# Revit family: Plumbing_Valves_Bermad_750-80_Level_Control_Valve_with_Altitude Pilot Threaded 1.5in-3in
name_source: partatom
category: Pipe Accessories
units: mm (PartAtom-declared; Revit-internal decimal feet)

## family parameters
Always vertical = Yes
Cut with Voids When Loaded = No
Part Type = Valve - Breaks Into
Round Connector Dimension = Use Diameter
Shared = No
Work Plane-Based = No

## types (4) — shared parameters
700EN = No
700ES = No
700Grooved = No
700Threaded = Yes
Act_Ang = 25.00°
Assembly Code = D2020300
D_Table = 700 Revit Sizes
D_Table_Version = 2
Date of publishing = 03/10/2019
Description = Level Control Valve with Altitude Pilot
HC = No
M = 160 mm
Manufacturer = Bermad
Max Working Water Pressure = 27.6 bar
Max Working Water Temperature = 60 °C
Model = 750-80
PA = No
PA_8 = Yes
PB = No
PBL = No
Port_Dim = 40 mm  [stored 0.131234 ft]
Product url = www.bermad.com/product/bc-750-80-p
Show Actuator Maintenance Space = No
T_from_port = 220 mm
URL = www.Bermad.com
Valve Seires = 700 Threaded

## per-type parameters (varying)
- 1.5" - DN40: Act_BD=119 mm; Ax=18 mm  [stored 0.0590551 ft]; Ay=80 mm  [stored 0.262467 ft]; Body_Dim=70 mm  [stored 0.229659 ft]; C_Plus=98 mm  [stored 0.321522 ft]; D1=86 mm  [stored 0.282152 ft]; D2=125 mm; D3=85 mm  [stored 0.278871 ft]; D4=125 mm; D5=86 mm  [stored 0.282152 ft]; D6=38 mm  [stored 0.124672 ft]; Flange_Dim=75 mm  [stored 0.246063 ft]; Flange_Thick=12 mm  [stored 0.0393701 ft]; H=201 mm; H1=10 mm  [stored 0.0328084 ft]; H2=19 mm  [stored 0.062336 ft]; H3=12 mm  [stored 0.0393701 ft]; H4=32 mm  [stored 0.104987 ft]; H5=9 mm  [stored 0.0295276 ft]; K Coefficient=3.1; L=155 mm; L_Half=78 mm  [stored 0.255906 ft]; Nominal Diameter=40 mm  [stored 0.131234 ft]; Port_Downx=36 mm  [stored 0.11811 ft]; Port_Upx=37 mm  [stored 0.121391 ft]; Port_W=41 mm  [stored 0.134514 ft]; Port_W2=81 mm  [stored 0.265748 ft]; Port_h=37 mm  [stored 0.121391 ft]; W=129 mm; Weight=0.05 kN; h=37 mm  [stored 0.121391 ft]
- 2" - DN50: Act_BD=119 mm; Ax=16 mm  [stored 0.0524934 ft]; Ay=82 mm  [stored 0.269029 ft]; Body_Dim=75 mm  [stored 0.246063 ft]; C_Plus=98 mm  [stored 0.321522 ft]; D1=86 mm  [stored 0.282152 ft]; D2=125 mm; D3=85 mm  [stored 0.278871 ft]; D4=125 mm; D5=86 mm  [stored 0.282152 ft]; D6=38 mm  [stored 0.124672 ft]; Flange_Dim=80 mm  [stored 0.262467 ft]; Flange_Thick=13 mm; H=203 mm; H1=10 mm  [stored 0.0328084 ft]; H2=19 mm  [stored 0.062336 ft]; H3=12 mm  [stored 0.0393701 ft]; H4=32 mm  [stored 0.104987 ft]; H5=9 mm  [stored 0.0295276 ft]; K Coefficient=5.4; L=155 mm; L_Half=78 mm  [stored 0.255906 ft]; Nominal Diameter=50 mm  [stored 0.164042 ft]; Port_Downx=37 mm  [stored 0.121391 ft]; Port_Upx=37 mm  [stored 0.121391 ft]; Port_W=41 mm  [stored 0.134514 ft]; Port_W2=81 mm  [stored 0.265748 ft]; Port_h=40 mm  [stored 0.131234 ft]; W=129 mm; Weight=0.05 kN; h=40 mm  [stored 0.131234 ft]
- 2.5" - DN65: Act_BD=119 mm; Ax=4 mm  [stored 0.0131234 ft]; Ay=82 mm  [stored 0.269029 ft]; Body_Dim=75 mm  [stored 0.246063 ft]; C_Plus=98 mm  [stored 0.321522 ft]; D1=86 mm  [stored 0.282152 ft]; D2=125 mm; D3=85 mm  [stored 0.278871 ft]; D4=125 mm; D5=86 mm  [stored 0.282152 ft]; D6=38 mm  [stored 0.124672 ft]; Flange_Dim=95 mm; Flange_Thick=16 mm  [stored 0.0524934 ft]; H=209 mm; H1=10 mm  [stored 0.0328084 ft]; H2=19 mm  [stored 0.062336 ft]; H3=12 mm  [stored 0.0393701 ft]; H4=32 mm  [stored 0.104987 ft]; H5=9 mm  [stored 0.0295276 ft]; K Coefficient=12.8; L=212 mm; L_Half=106 mm  [stored 0.347769 ft]; Nominal Diameter=65 mm  [stored 0.213255 ft]; Port_Downx=49 mm  [stored 0.160761 ft]; Port_Upx=49 mm  [stored 0.160761 ft]; Port_W=50 mm  [stored 0.164042 ft]; Port_W2=100 mm  [stored 0.328084 ft]; Port_h=41 mm  [stored 0.134514 ft]; W=129 mm; Weight=0.08 kN; h=48 mm  [stored 0.15748 ft]
- 3" - DN80: Act_BD=142 mm; Ax=14 mm  [stored 0.0459318 ft]; Ay=117 mm; Body_Dim=100 mm  [stored 0.328084 ft]; C_Plus=144 mm; D1=104 mm; D2=153 mm; D3=110 mm  [stored 0.360892 ft]; D4=165 mm; D5=124 mm; D6=42 mm  [stored 0.137795 ft]; Flange_Dim=110 mm  [stored 0.360892 ft]; Flange_Thick=28 mm  [stored 0.0918635 ft]; H=264 mm; H1=16 mm  [stored 0.0524934 ft]; H2=22 mm  [stored 0.0721785 ft]; H3=22 mm  [stored 0.0721785 ft]; H4=28 mm  [stored 0.0918635 ft]; H5=23 mm  [stored 0.0754593 ft]; K Coefficient=6.7; L=250 mm; L_Half=125 mm; Nominal Diameter=80 mm  [stored 0.262467 ft]; Port_Downx=68 mm  [stored 0.223097 ft]; Port_Upx=68 mm  [stored 0.223097 ft]; Port_W=58 mm  [stored 0.190289 ft]; Port_W2=116 mm; Port_h=56 mm  [stored 0.183727 ft]; W=163 mm; Weight=0.17 kN; h=56 mm  [stored 0.183727 ft]

note: [stored X ft] marks values corroborated as IEEE doubles in the binary element streams (Revit-internal decimal feet)

## geometry (parser evidence)
native form markers: Sweep x3
no freeform markers — native parametric forms only
